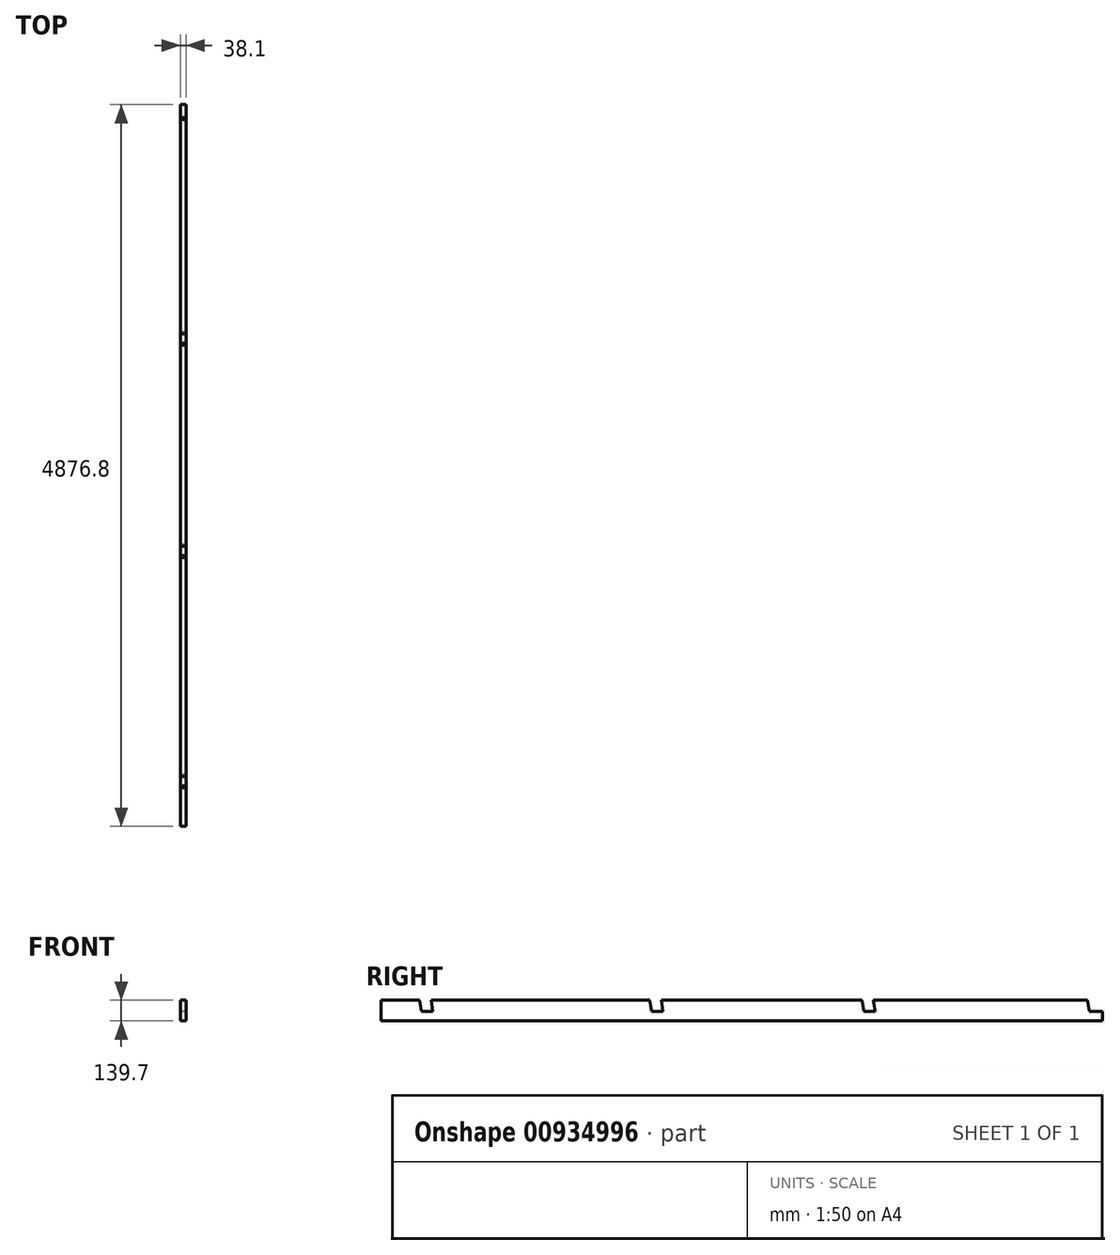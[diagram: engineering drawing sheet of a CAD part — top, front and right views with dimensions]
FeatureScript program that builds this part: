
annotation { "Feature Type Name" : "Feature", "Feature Type Description" : "" }
export const myFeature = defineFeature(function(context is Context, id is Id, definition is map)
    precondition{}
    {
        {
            var Q0;
            Q0=qCreatedBy(makeId("Front.planeOp"),FACE);
            var sketch = newSketch(context, id + "F0", { "sketchPlane" : qUnion([Q0])});
            skLineSegment(sketch, "E0.bottom", {"start": v(19.05, -69.85) * mm, "end": v(-19.05, -69.85) * mm});
            skLineSegment(sketch, "E0.top", {"start": v(19.05, 69.85) * mm, "end": v(-19.05, 69.85) * mm});
            skLineSegment(sketch, "E0.left", {"start": v(19.05, -69.85) * mm, "end": v(19.05, 69.85) * mm});
            skLineSegment(sketch, "E0.right", {"start": v(-19.05, -69.85) * mm, "end": v(-19.05, 69.85) * mm});
            skPoint(sketch, "E0.middle", {"position": v(0, 0) * mm});
            skSolve(sketch);
        }
        {
            var Q0;
            Q0 = qSketchRegion(id + "F0", true);
            extrude(context, id + "F1", {"entities" : qUnion([Q0]), "depth" : 4876.8 * mm, "offsetDistance" : 25.4 * mm});
        }
        {
            var Q0;
            Q0=makeQuery(id+"F1.opExtrude","SWEPT_FACE",FACE,{"disambiguationData":[OSD([sQuery(id+"F0.wireOp",EDGE,"E0.right")])]});
            var sketch = newSketch(context, id + "F2", { "sketchPlane" : qUnion([Q0])});
            skLineSegment(sketch, "E1.bottom", {"start": v(1548.39, 69.85) * mm, "end": v(1625.6, 69.85) * mm});
            skLineSegment(sketch, "E1.top", {"start": v(1536.07, -5.35) * mm, "end": v(1613.29, -5.35) * mm});
            skLineSegment(sketch, "E1.left", {"start": v(1548.39, 69.85) * mm, "end": v(1536.07, -5.35) * mm});
            skLineSegment(sketch, "E1.right", {"start": v(1625.6, 69.85) * mm, "end": v(1613.29, -5.35) * mm});
            skLineSegment(sketch, "E2.bottom", {"start": v(2983.49, 69.85) * mm, "end": v(3060.7, 69.85) * mm});
            skLineSegment(sketch, "E2.top", {"start": v(2971.17, -5.35) * mm, "end": v(3048.39, -5.35) * mm});
            skLineSegment(sketch, "E2.left", {"start": v(2983.49, 69.85) * mm, "end": v(2971.17, -5.35) * mm});
            skLineSegment(sketch, "E2.right", {"start": v(3060.7, 69.85) * mm, "end": v(3048.39, -5.35) * mm});
            skLineSegment(sketch, "E3.bottom", {"start": v(4539.24, 69.85) * mm, "end": v(4616.45, 69.85) * mm});
            skLineSegment(sketch, "E3.top", {"start": v(4526.92, -5.35) * mm, "end": v(4604.14, -5.35) * mm});
            skLineSegment(sketch, "E3.left", {"start": v(4539.24, 69.85) * mm, "end": v(4526.92, -5.35) * mm});
            skLineSegment(sketch, "E3.right", {"start": v(4616.45, 69.85) * mm, "end": v(4604.14, -5.35) * mm});
            skLineSegment(sketch, "E4", {"start": v(101.6, 69.85) * mm, "end": v(89.29, -5.35) * mm});
            skLineSegment(sketch, "E5", {"start": v(89.29, -5.35) * mm, "end": v(0, -5.35) * mm});
            skLineSegment(sketch, "E6", {"start": v(0, -5.35) * mm, "end": v(0, 69.85) * mm});
            skLineSegment(sketch, "E7", {"start": v(0, 69.85) * mm, "end": v(101.6, 69.85) * mm});
            skSolve(sketch);
        }
        {
            var Q0;
            Q0 = qSketchRegion(id + "F2", true);
            extrude(context, id + "F3", {"entities" : qUnion([Q0]), "operationType" : NewBodyOperationType.REMOVE, "oppositeDirection" : true, "depth" : 254 * mm, "offsetDistance" : 25.4 * mm, "symmetric" : true});
        }
    });
